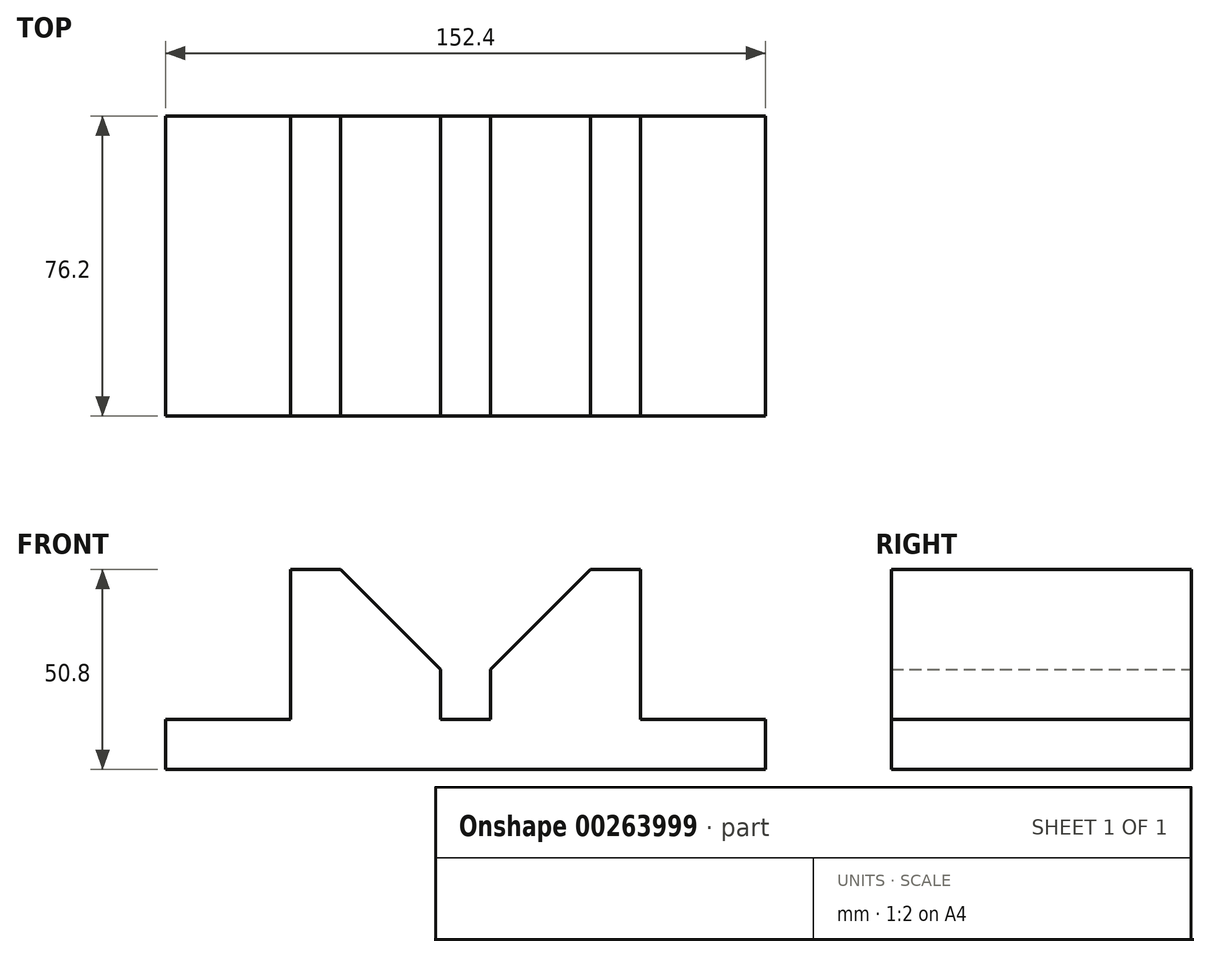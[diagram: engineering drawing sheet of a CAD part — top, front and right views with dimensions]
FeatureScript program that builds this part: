
annotation { "Feature Type Name" : "Feature", "Feature Type Description" : "" }
export const myFeature = defineFeature(function(context is Context, id is Id, definition is map)
    precondition{}
    {
        {
            var Q0;
            Q0=qCreatedBy(makeId("Front.planeOp"),FACE);
            var sketch = newSketch(context, id + "F0", { "sketchPlane" : qUnion([Q0])});
            skLineSegment(sketch, "E0", {"start": v(-76.84, 12.7) * mm, "end": v(-76.84, 0) * mm});
            skLineSegment(sketch, "E1", {"start": v(-76.84, 12.7) * mm, "end": v(-45.1, 12.7) * mm});
            skLineSegment(sketch, "E2", {"start": v(-76.84, 0) * mm, "end": v(75.56, 0) * mm});
            skLineSegment(sketch, "E3", {"start": v(75.56, 0) * mm, "end": v(75.56, 12.7) * mm});
            skLineSegment(sketch, "E4", {"start": v(75.56, 12.7) * mm, "end": v(43.8, 12.7) * mm});
            skLineSegment(sketch, "E5", {"start": v(-45.1, 12.7) * mm, "end": v(-45.1, 50.8) * mm});
            skLineSegment(sketch, "E6", {"start": v(43.8, 12.7) * mm, "end": v(43.8, 50.8) * mm});
            skLineSegment(sketch, "E7", {"start": v(-45.1, 50.8) * mm, "end": v(-32.4, 50.8) * mm});
            skLineSegment(sketch, "E8", {"start": v(43.8, 50.8) * mm, "end": v(31.1, 50.8) * mm});
            skLineSegment(sketch, "E9", {"start": v(-7, 12.7) * mm, "end": v(-7, 25.4) * mm});
            skLineSegment(sketch, "E10", {"start": v(-7, 25.4) * mm, "end": v(-32.4, 50.8) * mm});
            skLineSegment(sketch, "E11", {"start": v(-7, 12.7) * mm, "end": v(5.7, 12.7) * mm});
            skLineSegment(sketch, "E12", {"start": v(5.7, 12.7) * mm, "end": v(5.7, 25.4) * mm});
            skLineSegment(sketch, "E13", {"start": v(5.7, 25.4) * mm, "end": v(31.1, 50.8) * mm});
            skSolve(sketch);
        }
        {
            var Q0;
            Q0=makeQuery(id+"F0.imprint","IMPRINT",FACE,{"disambiguationData":[TD([[makeQuery(id+"F0.imprint","IMPRINT",EDGE,{"derivedFrom":sQuery(id+"F0.wireOp",EDGE,"E0")}),1.0]])]});
            extrude(context, id + "F1", {"entities" : qUnion([Q0]), "depth" : 76.2 * mm});
        }
    });
